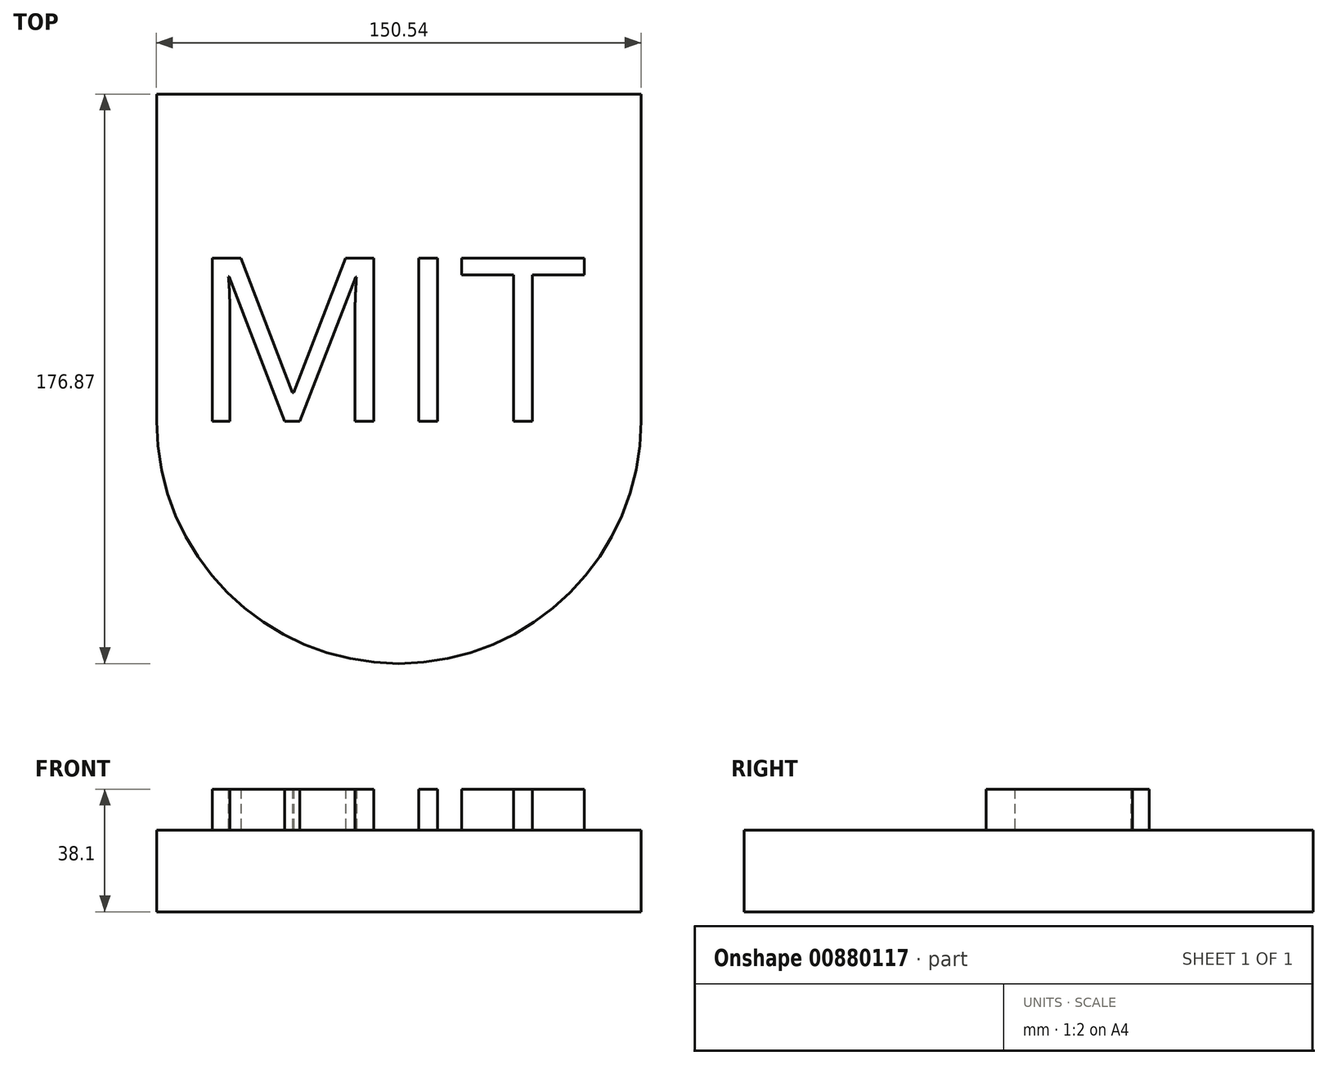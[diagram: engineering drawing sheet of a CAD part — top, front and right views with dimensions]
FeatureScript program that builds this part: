
annotation { "Feature Type Name" : "Feature", "Feature Type Description" : "" }
export const myFeature = defineFeature(function(context is Context, id is Id, definition is map)
    precondition{}
    {
        {
            var Q0;
            Q0=qCreatedBy(makeId("Top.planeOp"),FACE);
            var sketch = newSketch(context, id + "F0", { "sketchPlane" : qUnion([Q0])});
            skArc(sketch, "E0", {"start": v(-75.27, 0) * mm, "mid": v(0, -75.27) * mm, "end": v(75.27, 0) * mm});
            skLineSegment(sketch, "E1.top", {"start": v(-75.27, 101.6) * mm, "end": v(75.27, 101.6) * mm});
            skLineSegment(sketch, "E1.left", {"start": v(-75.27, 0) * mm, "end": v(-75.27, 101.6) * mm});
            skLineSegment(sketch, "E1.right", {"start": v(75.27, 0) * mm, "end": v(75.27, 101.6) * mm});
            skLineSegment(sketch, "E2.trimOffspring", {"start": v(75.27, 0) * mm, "end": v(75.27, 0) * mm});
            skSolve(sketch);
        }
        {
            var Q0;
            Q0=makeQuery(id+"F0.imprint","IMPRINT",FACE,{"disambiguationData":[TD([[makeQuery(id+"F0.imprint","IMPRINT",EDGE,{"derivedFrom":sQuery(id+"F0.wireOp",EDGE,"E0")}),1.0]])]});
            extrude(context, id + "F1", {"entities" : qUnion([Q0]), "depth" : 25.4 * mm, "offsetDistance" : 25.4 * mm});
        }
        {
            var Q0;
            Q0=makeQuery(id+"F1.opExtrude","CAP_FACE",FACE,{"disambiguationData":[OSD([sQuery(id+"F0.wireOp",EDGE,"E0"),sQuery(id+"F0.wireOp",EDGE,"E1.top"),sQuery(id+"F0.wireOp",EDGE,"E1.left"),sQuery(id+"F0.wireOp",EDGE,"E1.right")])],"isStart":false});
            var sketch = newSketch(context, id + "F2", { "sketchPlane" : qUnion([Q0])});
            skText(sketch, "E3", { "text": "MIT", "fontName": "OpenSans-Regular.ttf"});
            skPoint(sketch, "E4", {"position": v(-75.27, 50.8) * mm});
            const initialGuessF2  = {"E3": [-0.06486, 0, 1, 0, 0.05109]};
            skSetInitialGuess(sketch, initialGuessF2);
            skSolve(sketch);
        }
        {
            var Q0;
            Q0 = qSketchRegion(id + "F2", true);
            extrude(context, id + "F3", {"entities" : qUnion([Q0]), "operationType" : NewBodyOperationType.ADD, "depth" : 12.7 * mm, "offsetDistance" : 25.4 * mm});
        }
    });
